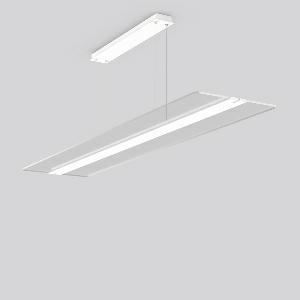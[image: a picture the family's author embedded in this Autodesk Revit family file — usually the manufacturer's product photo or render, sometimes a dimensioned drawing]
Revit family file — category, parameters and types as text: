
# Revit family: twindot_s_312265_002_1_fde0
name_source: partatom
category: Lighting Fixtures
units: mm (PartAtom-declared; Revit-internal decimal feet)

## family parameters
Cut with Voids When Loaded = No
Host = Face
Light Source = No
Part Type = Normal
Room Calculation Point = No
Round Connector Dimension = Use Diameter
Shared = No

## types (1)
- TWINDOT S (1 x LED Modul 840, 8100 lm, 4000)
    Apparent Load = 62 VA
    CIE Flux Codes = 47 77 94 55 100
    Color Rendering = 80
    Color Temperature = 4000
    Default Elevation = 1800 mm
    Description = Series: TWINDOT S
LED pendant luminaire with extremely flat and frameless appearance. Middle bar made of aluminium extrusion profile, powder-coated. Transparent light guide made of UV-resistant acrylic glass (PMMA) with TWINDOT prismatic. Light control with perfectly glare-free TWINDOT technology for pleasantly gentle light with soft shadows. Even and wide indirect and direct light distribution. Direct 55%, indirect 45% light emission. 4-point steel cable suspension, steplessly adjustable. Converter integrated in the canopy (powder-coated white). Power supply through suspension cable. 
Colour: traffic white, matt (RAL 9016)
Length: 1500 mm
Width: 350 mm
Height: 20 mm
Suspension length: 500-1200 mm
Lamp: LED
Socket: without socket
Colour temperature: 4000K
Colour rendering index (CRI): 80
System power: 62 W
Rated luminous flux: 8100 lm
Luminous efficiency: 131 lm/W
Control gear: Regulated power supply
Protection class: I
Type of protection: IP 20
    Height = 20 mm  [stored 0.0656168 ft]
    Lamp = 1 x LED Modul 840
    Lamp Light Flux = 8100 lm
    Lamp count = 1
    Length = 1500 mm
    Lifetime = 50000 h
    Luminous efficacy = 131 lm/W
    Manufacturer = RZB
    ModVariant = No
    Model = 312265.002.1
    Mounting Place = Ceiling
    Mounting Type = Pendant
    Number of Poles = 1
    OnlyDefault = Yes
    Power Factor = 1
    Product Name = TWINDOT S
    Product group = Pendant modular luminaires
    ProductGroupID = 906
    Protection Class = Protection class I
    Protection Degree = IP 20
    RLX_Detail_Level = 1
    RLX_Emergency_Light_Flux = 0 lm
    RLX_Emergency_Type = 0
    RLX_Emergency_Type_DB = No
    RlxData = <blob elided: 36649 chars, md5=10653d9a>
    Socket = socket
    Standby Power = 0 W
    System Light Flux = 8100 lm
    System Power = 62 W
    Type Comments = Product without accessories
    Type Image = 312265.002.jpg
    URL = http://relux.com
    VarID = ---
    Voltage = 230 V
    Voltage Range = 220-240 V
    Weight = 0.00 kg
    Width = 350 mm

note: [stored X ft] marks values corroborated as IEEE doubles in the binary element streams (Revit-internal decimal feet)

## geometry (parser evidence)
native form markers: Blend x4, Sweep x11
no freeform markers — native parametric forms only
